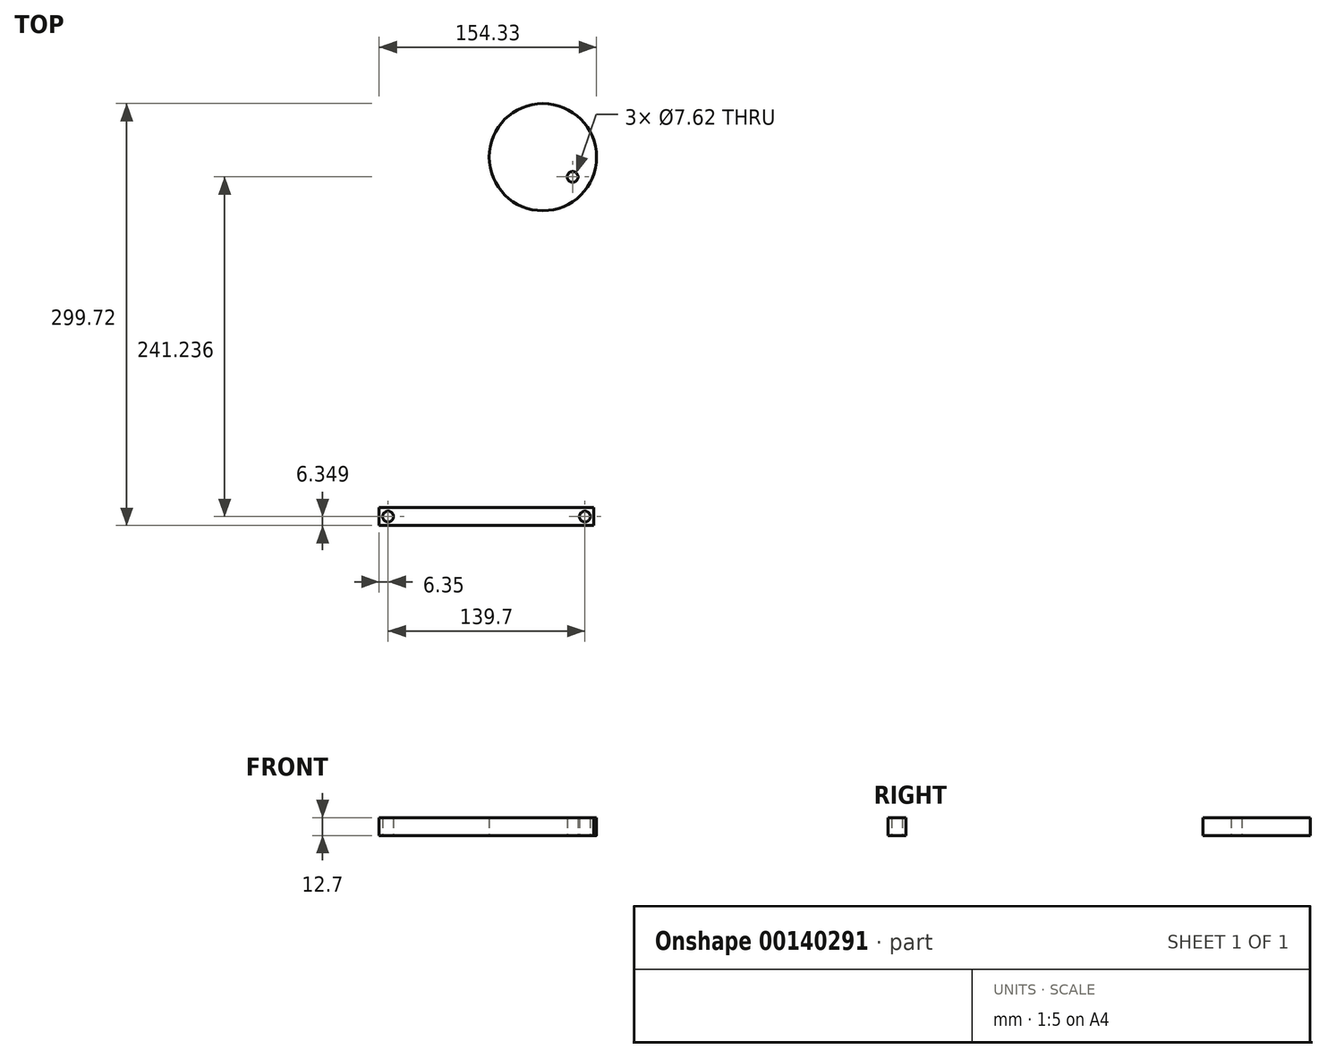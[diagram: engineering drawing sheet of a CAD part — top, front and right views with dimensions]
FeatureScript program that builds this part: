
annotation { "Feature Type Name" : "Feature", "Feature Type Description" : "" }
export const myFeature = defineFeature(function(context is Context, id is Id, definition is map)
    precondition{}
    {
        {
            var Q0;
            Q0=qCreatedBy(makeId("Top.planeOp"),FACE);
            var sketch = newSketch(context, id + "F0", { "sketchPlane" : qUnion([Q0])});
            skLineSegment(sketch, "E0.bottom", {"start": v(-91.2, -2.28) * mm, "end": v(61.2, -2.28) * mm});
            skLineSegment(sketch, "E0.top", {"start": v(-91.2, -14.98) * mm, "end": v(61.2, -14.98) * mm});
            skLineSegment(sketch, "E0.left", {"start": v(-91.2, -2.28) * mm, "end": v(-91.2, -14.98) * mm});
            skLineSegment(sketch, "E0.right", {"start": v(61.2, -2.28) * mm, "end": v(61.2, -14.98) * mm});
            skLineSegment(sketch, "E1.bottom", {"start": v(-91.2, -2.28) * mm, "end": v(-78.5, -2.28) * mm});
            skLineSegment(sketch, "E1.top", {"start": v(-91.2, -14.98) * mm, "end": v(-78.5, -14.98) * mm});
            skCircle(sketch, "E2", {"center": v(-84.86, -8.63) * mm, "radius": 3.81 * mm});
            skLineSegment(sketch, "E3.bottom", {"start": v(61.2, -2.28) * mm, "end": v(48.5, -2.28) * mm});
            skLineSegment(sketch, "E3.top", {"start": v(61.2, -14.98) * mm, "end": v(48.5, -14.98) * mm});
            skCircle(sketch, "E4", {"center": v(54.84, -8.63) * mm, "radius": 3.81 * mm});
            skSolve(sketch);
        }
        {
            var Q0;
            Q0=makeQuery(id+"F0.imprint","IMPRINT",FACE,{"disambiguationData":[TD([[makeQuery(id+"F0.imprint","IMPRINT",EDGE,{"derivedFrom":sQuery(id+"F0.wireOp",EDGE,"E0.bottom")}),-1.0]])]});
            extrude(context, id + "F1", {"entities" : qUnion([Q0]), "depth" : 12.7 * mm});
        }
        {
            var Q0;
            Q0=qCreatedBy(makeId("Top.planeOp"),FACE);
            var sketch = newSketch(context, id + "F2", { "sketchPlane" : qUnion([Q0])});
            skCircle(sketch, "E5", {"center": v(25.02, 246.64) * mm, "radius": 38.1 * mm});
            skLineSegment(sketch, "E6", {"start": v(56.94, 225.83) * mm, "end": v(46.2, 232.6) * mm});
            skCircle(sketch, "E7", {"center": v(46.2, 232.6) * mm, "radius": 3.81 * mm});
            skSolve(sketch);
        }
        {
            var Q0;
            Q0=makeQuery(id+"F2.imprint","IMPRINT",FACE,{"disambiguationData":[TD([[makeQuery(id+"F2.imprint","IMPRINT",EDGE,{"derivedFrom":sQuery(id+"F2.wireOp",EDGE,"E5")}),1.0]])]});
            extrude(context, id + "F3", {"entities" : qUnion([Q0]), "depth" : 12.7 * mm});
        }
    });
